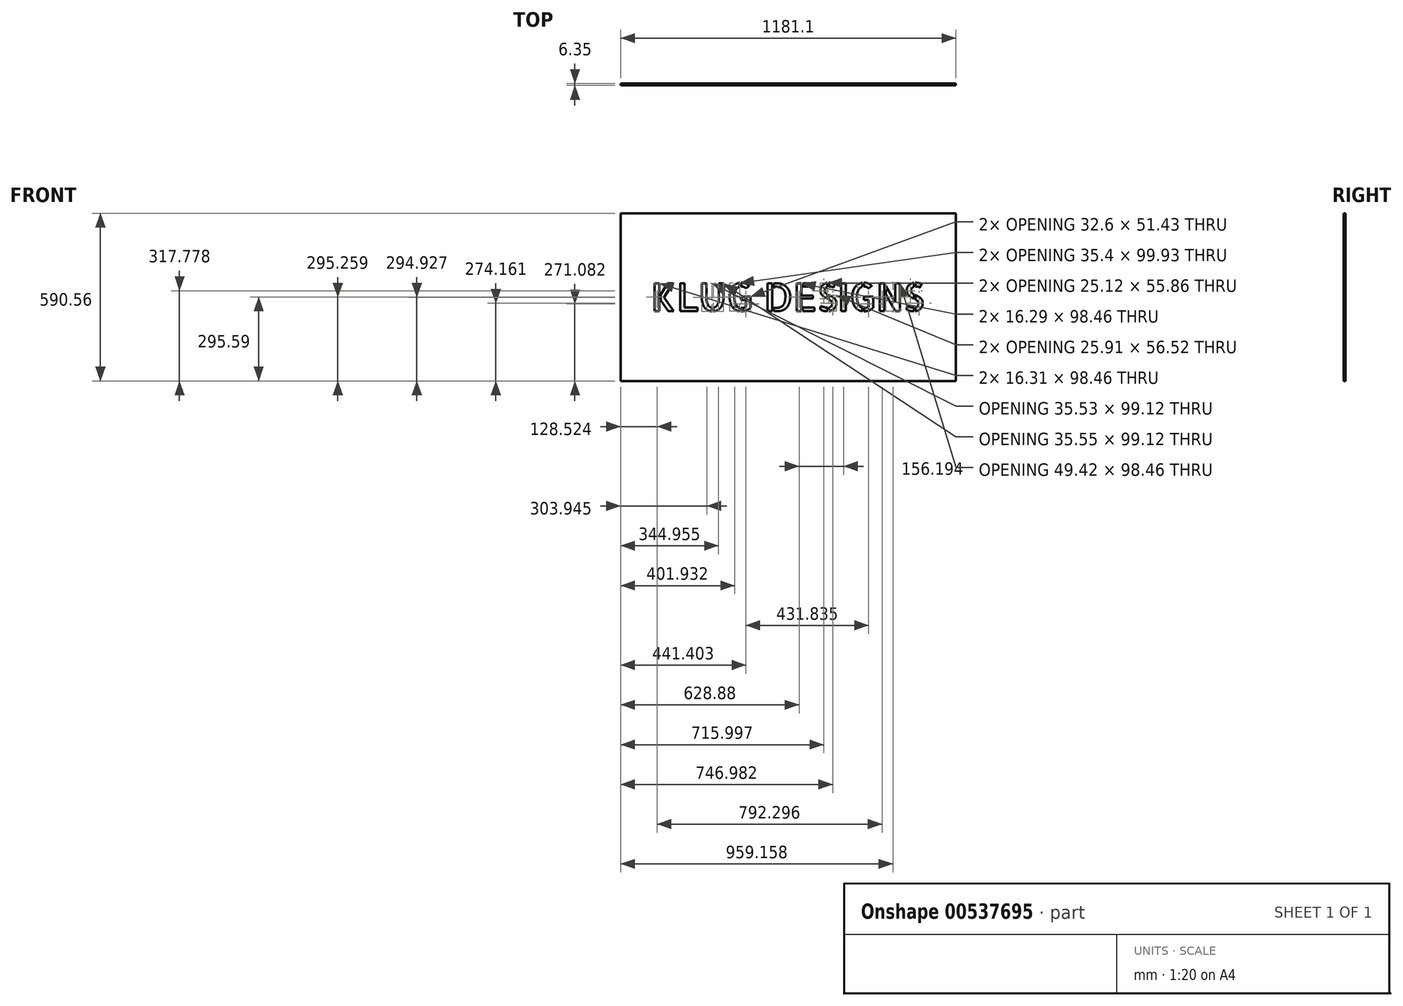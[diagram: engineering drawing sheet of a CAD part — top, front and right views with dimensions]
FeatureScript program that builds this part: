
annotation { "Feature Type Name" : "Feature", "Feature Type Description" : "" }
export const myFeature = defineFeature(function(context is Context, id is Id, definition is map)
    precondition{}
    {
        {
            var Q0;
            Q0=qCreatedBy(makeId("Front.planeOp"),FACE);
            var sketch = newSketch(context, id + "F0", { "sketchPlane" : qUnion([Q0])});
            skLineSegment(sketch, "E0.bottom", {"start": v(-590.55, -295.28) * mm, "end": v(590.55, -295.28) * mm});
            skLineSegment(sketch, "E0.top", {"start": v(-590.55, 295.28) * mm, "end": v(590.55, 295.28) * mm});
            skLineSegment(sketch, "E0.left", {"start": v(-590.55, -295.28) * mm, "end": v(-590.55, 295.28) * mm});
            skLineSegment(sketch, "E0.right", {"start": v(590.55, -295.28) * mm, "end": v(590.55, 295.28) * mm});
            skPoint(sketch, "E0.middle", {"position": v(0, 0) * mm});
            skSolve(sketch);
        }
        {
            var Q0;
            Q0 = qSketchRegion(id + "F0", true);
            extrude(context, id + "F1", {"entities" : qUnion([Q0]), "depth" : 6.35 * mm, "offsetDistance" : 25.4 * mm});
        }
        {
            var Q0;
            Q0=makeQuery(id+"F1.opExtrude","CAP_FACE",FACE,{"disambiguationData":[OSD([sQuery(id+"F0.wireOp",EDGE,"E0.bottom"),sQuery(id+"F0.wireOp",EDGE,"E0.top"),sQuery(id+"F0.wireOp",EDGE,"E0.left"),sQuery(id+"F0.wireOp",EDGE,"E0.right")])],"isStart":false});
            var sketch = newSketch(context, id + "F2", { "sketchPlane" : qUnion([Q0])});
            skText(sketch, "E1", { "text": "KLUG DESIGNS", "fontName": "AllertaStencil-Regular.ttf"});
            skLineSegment(sketch, "E2", {"start": v(-482.6, 0) * mm, "end": v(482.6, 0) * mm, "construction": true});
            const initialGuessF2  = {"E1": [-0.4826, -0.04925, 1, 0, 0.0985]};
            skSetInitialGuess(sketch, initialGuessF2);
            skSolve(sketch);
        }
        {
            var Q0;
            Q0 = qSketchRegion(id + "F2", true);
            extrude(context, id + "F3", {"entities" : qUnion([Q0]), "operationType" : NewBodyOperationType.REMOVE, "endBound" : BoundingType.THROUGH_ALL, "oppositeDirection" : true, "depth" : 25.4 * mm, "offsetDistance" : 25.4 * mm});
        }
    });
